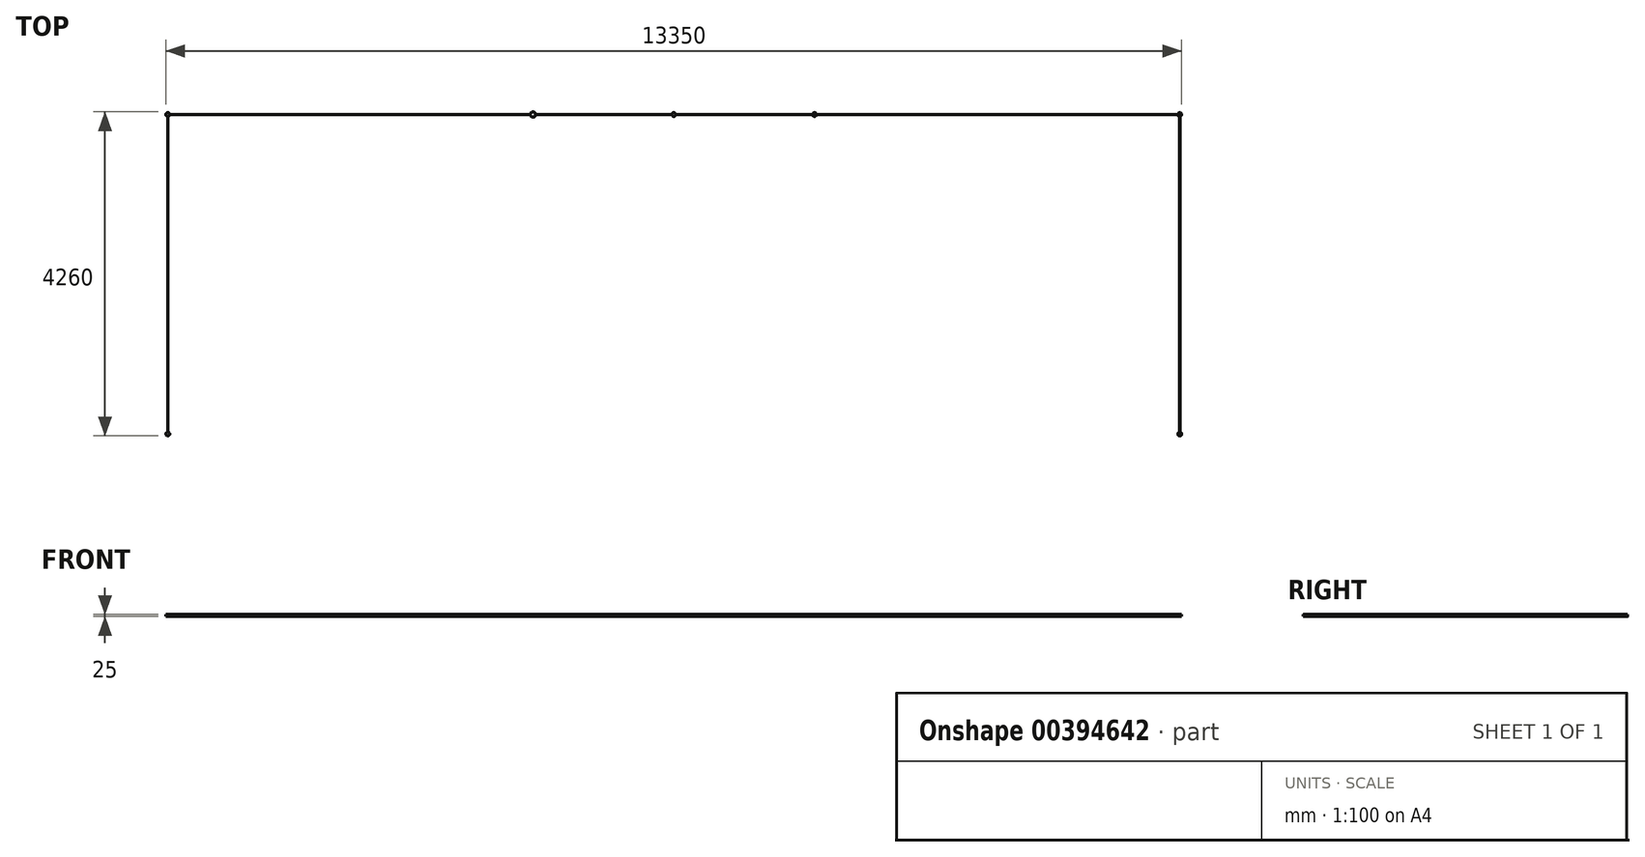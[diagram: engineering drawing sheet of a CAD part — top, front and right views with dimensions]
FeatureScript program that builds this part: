
annotation { "Feature Type Name" : "Feature", "Feature Type Description" : "" }
export const myFeature = defineFeature(function(context is Context, id is Id, definition is map)
    precondition{}
    {
        {
            var Q0;
            Q0=qCreatedBy(makeId("Top.planeOp"),FACE);
            var sketch = newSketch(context, id + "F0", { "sketchPlane" : qUnion([Q0])});
            skLineSegment(sketch, "E0", {"start": v(0, 0) * mm, "end": v(-1850, 0) * mm, "construction": true});
            skLineSegment(sketch, "E1", {"start": v(-1850, 0) * mm, "end": v(-6650, 0) * mm, "construction": true});
            skLineSegment(sketch, "E2", {"start": v(0, 0) * mm, "end": v(1850, 0) * mm, "construction": true});
            skLineSegment(sketch, "E3", {"start": v(1850, 0) * mm, "end": v(6650, 0) * mm, "construction": true});
            skLineSegment(sketch, "E4", {"start": v(1850, 0) * mm, "end": v(4250, 4156.92) * mm, "construction": true});
            skLineSegment(sketch, "E5", {"start": v(4250, 4156.92) * mm, "end": v(6650, 0) * mm, "construction": true});
            skLineSegment(sketch, "E6", {"start": v(6650, 0) * mm, "end": v(4250, -4156.92) * mm, "construction": true});
            skLineSegment(sketch, "E7", {"start": v(4250, -4156.92) * mm, "end": v(1850, 0) * mm, "construction": true});
            skLineSegment(sketch, "E8", {"start": v(-6650, 0) * mm, "end": v(-4250, 4156.92) * mm, "construction": true});
            skLineSegment(sketch, "E9", {"start": v(-4250, 4156.92) * mm, "end": v(-1850, 0) * mm, "construction": true});
            skLineSegment(sketch, "E10", {"start": v(-1850, 0) * mm, "end": v(-4250, -4156.92) * mm, "construction": true});
            skLineSegment(sketch, "E11", {"start": v(-4250, -4156.92) * mm, "end": v(-6650, 0) * mm, "construction": true});
            skCircle(sketch, "E12", {"center": v(-1850, 0) * mm, "radius": 35 * mm});
            skCircle(sketch, "E13", {"center": v(1850, 0) * mm, "radius": 25 * mm});
            skPoint(sketch, "E14", {"position": v(-4250, 4156.92) * mm});
            skPoint(sketch, "E15", {"position": v(-6650, 0) * mm});
            skPoint(sketch, "E16", {"position": v(-4250, -4156.92) * mm});
            skPoint(sketch, "E17", {"position": v(4250, -4156.92) * mm});
            skPoint(sketch, "E18", {"position": v(6650, 0) * mm});
            skPoint(sketch, "E19", {"position": v(4250, 4156.92) * mm});
            skCircle(sketch, "E20", {"center": v(-6650, 0) * mm, "radius": 25 * mm});
            skLineSegment(sketch, "E21.0.left", {"start": v(-24.87, -2.5) * mm, "end": v(-1815.09, -2.5) * mm});
            skLineSegment(sketch, "E21.0.right", {"start": v(-24.87, 2.5) * mm, "end": v(-1815.09, 2.5) * mm});
            skLineSegment(sketch, "E21.1.left", {"start": v(24.87, 2.5) * mm, "end": v(1825.13, 2.5) * mm});
            skLineSegment(sketch, "E21.1.right", {"start": v(24.87, -2.5) * mm, "end": v(1825.13, -2.5) * mm});
            skCircle(sketch, "E22", {"center": v(6650, 0) * mm, "radius": 25 * mm});
            skLineSegment(sketch, "E23", {"start": v(6650, 0) * mm, "end": v(6650, -4200) * mm, "construction": true});
            skLineSegment(sketch, "E24", {"start": v(-6650, 0) * mm, "end": v(-6650, -4200) * mm, "construction": true});
            skCircle(sketch, "E25", {"center": v(-6650, -4200) * mm, "radius": 25 * mm});
            skCircle(sketch, "E26", {"center": v(6650, -4200) * mm, "radius": 25 * mm});
            skLineSegment(sketch, "E27.0.left", {"start": v(6652.5, -24.87) * mm, "end": v(6652.5, -4175.13) * mm});
            skArc(sketch, "E27.1.endCap", {"start": v(-6647.5, -4200) * mm, "mid": v(-6650, -4202.5) * mm, "end": v(-6652.5, -4200) * mm});
            skLineSegment(sketch, "E27.1.left", {"start": v(-6647.5, -24.87) * mm, "end": v(-6647.5, -4200) * mm});
            skLineSegment(sketch, "E27.1.right", {"start": v(-6652.5, -24.87) * mm, "end": v(-6652.5, -4200) * mm});
            skLineSegment(sketch, "E28.trimOffspring", {"start": v(6647.5, -24.87) * mm, "end": v(6647.5, -4175.13) * mm});
            skLineSegment(sketch, "E29.trimOffspring", {"start": v(1874.94, 1.79) * mm, "end": v(6625.13, 2.5) * mm});
            skLineSegment(sketch, "E30.trimOffspring", {"start": v(1874.94, -1.79) * mm, "end": v(6625.13, -2.5) * mm});
            skCircle(sketch, "E31", {"center": v(0, 0) * mm, "radius": 25 * mm});
            skLineSegment(sketch, "E32.trimOffspring", {"start": v(-1884.91, 2.5) * mm, "end": v(-6625.13, 2.5) * mm});
            skLineSegment(sketch, "E33.trimOffspring", {"start": v(-1884.91, -2.5) * mm, "end": v(-6625.13, -2.5) * mm});
            skPoint(sketch, "E27.0.endCap.end.orphan", {"position": v(6647.5, -4200) * mm});
            skPoint(sketch, "E27.0.endCap.start.orphan", {"position": v(6652.5, -4200) * mm});
            skSolve(sketch);
        }
        {
            var Q0;
            {var subQ0=sQuery(id+"F0.wireOp",EDGE,"E21.0.left");Q0=makeQuery(id+"F0.imprint","IMPRINT",FACE,{"disambiguationData":[TD([[makeQuery(id+"F0.imprint","IMPRINT",EDGE,{"derivedFrom":subQ0}),-1.0]])]});}
            var Q1;
            {var subQ0=sQuery(id+"F0.wireOp",EDGE,"E32.trimOffspring");Q1=makeQuery(id+"F0.imprint","IMPRINT",FACE,{"disambiguationData":[TD([[makeQuery(id+"F0.imprint","IMPRINT",EDGE,{"derivedFrom":subQ0}),1.0]])]});}
            var Q2;
            {var subQ0=sQuery(id+"F0.wireOp",EDGE,"E27.1.left");var subQ1=sQuery(id+"F0.wireOp",EDGE,"E20");var subQ2=makeQuery(id+"F0.imprint","INTERSECT",VERTEX,{"derivedFrom":[subQ1,subQ0]});Q2=makeQuery(id+"F0.imprint","IMPRINT",FACE,{"disambiguationData":[TD([[makeQuery(id+"F0.imprint","IMPRINT",EDGE,{"disambiguationData":[TD([[subQ2,1.0]])],"derivedFrom":subQ1}),-1.0]])]});}
            var Q3;
            {var subQ0=sQuery(id+"F0.wireOp",EDGE,"E21.1.left");Q3=makeQuery(id+"F0.imprint","IMPRINT",FACE,{"disambiguationData":[TD([[makeQuery(id+"F0.imprint","IMPRINT",EDGE,{"derivedFrom":subQ0}),-1.0]])]});}
            var Q4;
            {var subQ0=sQuery(id+"F0.wireOp",EDGE,"E29.trimOffspring");Q4=makeQuery(id+"F0.imprint","IMPRINT",FACE,{"disambiguationData":[TD([[makeQuery(id+"F0.imprint","IMPRINT",EDGE,{"derivedFrom":subQ0}),-1.0]])]});}
            var Q5;
            {var subQ0=sQuery(id+"F0.wireOp",EDGE,"E27.0.left");Q5=makeQuery(id+"F0.imprint","IMPRINT",FACE,{"disambiguationData":[TD([[makeQuery(id+"F0.imprint","IMPRINT",EDGE,{"derivedFrom":subQ0}),-1.0]])]});}
            extrude(context, id + "F1", {"entities" : qUnion([Q0, Q1, Q2, Q3, Q4, Q5]), "depth" : 25 * mm, "offsetDistance" : 25 * mm});
        }
        {
            var Q0;
            {var subQ5=sQuery(id+"F0.wireOp",EDGE,"E27.1.endCap");Q0=makeQuery(id+"F0.imprint","IMPRINT",FACE,{"disambiguationData":[TD([[makeQuery(id+"F0.imprint","IMPRINT",EDGE,{"derivedFrom":subQ5}),1.0]])]});}
            var Q1;
            {var subQ5=sQuery(id+"F0.wireOp",EDGE,"E27.1.endCap");Q1=makeQuery(id+"F0.imprint","IMPRINT",FACE,{"disambiguationData":[TD([[makeQuery(id+"F0.imprint","IMPRINT",EDGE,{"derivedFrom":subQ5}),-1.0]])]});}
            var Q2;
            {var subQ0=sQuery(id+"F0.wireOp",EDGE,"E20");var subQ1=makeQuery(id+"F0.imprint","INTERSECT",VERTEX,{"derivedFrom":[subQ0,sQuery(id+"F0.wireOp",EDGE,"E27.1.right")]});Q2=makeQuery(id+"F0.imprint","IMPRINT",FACE,{"disambiguationData":[TD([[makeQuery(id+"F0.imprint","IMPRINT",EDGE,{"disambiguationData":[TD([[subQ1,1.0]])],"derivedFrom":subQ0}),1.0]])]});}
            var Q3;
            {var subQ0=sQuery(id+"F0.wireOp",EDGE,"E12");var subQ1=makeQuery(id+"F0.imprint","INTERSECT",VERTEX,{"derivedFrom":[subQ0,sQuery(id+"F0.wireOp",EDGE,"E21.0.right")]});Q3=makeQuery(id+"F0.imprint","IMPRINT",FACE,{"disambiguationData":[TD([[makeQuery(id+"F0.imprint","IMPRINT",EDGE,{"disambiguationData":[TD([[subQ1,-1.0]])],"derivedFrom":subQ0}),1.0]])]});}
            var Q4;
            {var subQ0=sQuery(id+"F0.wireOp",EDGE,"E31");var subQ1=makeQuery(id+"F0.imprint","INTERSECT",VERTEX,{"derivedFrom":[sQuery(id+"F0.wireOp",EDGE,"E21.0.right"),subQ0]});Q4=makeQuery(id+"F0.imprint","IMPRINT",FACE,{"disambiguationData":[TD([[makeQuery(id+"F0.imprint","IMPRINT",EDGE,{"disambiguationData":[TD([[subQ1,1.0]])],"derivedFrom":subQ0}),1.0]])]});}
            var Q5;
            {var subQ0=sQuery(id+"F0.wireOp",EDGE,"E13");var subQ1=makeQuery(id+"F0.imprint","INTERSECT",VERTEX,{"derivedFrom":[subQ0,sQuery(id+"F0.wireOp",EDGE,"E21.1.left")]});Q5=makeQuery(id+"F0.imprint","IMPRINT",FACE,{"disambiguationData":[TD([[makeQuery(id+"F0.imprint","IMPRINT",EDGE,{"disambiguationData":[TD([[subQ1,1.0]])],"derivedFrom":subQ0}),1.0]])]});}
            var Q6;
            {var subQ0=sQuery(id+"F0.wireOp",EDGE,"E22");var subQ1=makeQuery(id+"F0.imprint","INTERSECT",VERTEX,{"derivedFrom":[subQ0,sQuery(id+"F0.wireOp",EDGE,"E29.trimOffspring")]});Q6=makeQuery(id+"F0.imprint","IMPRINT",FACE,{"disambiguationData":[TD([[makeQuery(id+"F0.imprint","IMPRINT",EDGE,{"disambiguationData":[TD([[subQ1,-1.0]])],"derivedFrom":subQ0}),1.0]])]});}
            var Q7;
            {var subQ0=sQuery(id+"F0.wireOp",EDGE,"E26");var subQ1=makeQuery(id+"F0.imprint","INTERSECT",VERTEX,{"derivedFrom":[subQ0,sQuery(id+"F0.wireOp",EDGE,"E27.0.left")]});Q7=makeQuery(id+"F0.imprint","IMPRINT",FACE,{"disambiguationData":[TD([[makeQuery(id+"F0.imprint","IMPRINT",EDGE,{"disambiguationData":[TD([[subQ1,-1.0]])],"derivedFrom":subQ0}),1.0]])]});}
            extrude(context, id + "F2", {"entities" : qUnion([Q0, Q1, Q2, Q3, Q4, Q5, Q6, Q7]), "depth" : 25 * mm, "offsetDistance" : 25 * mm});
        }
    });
